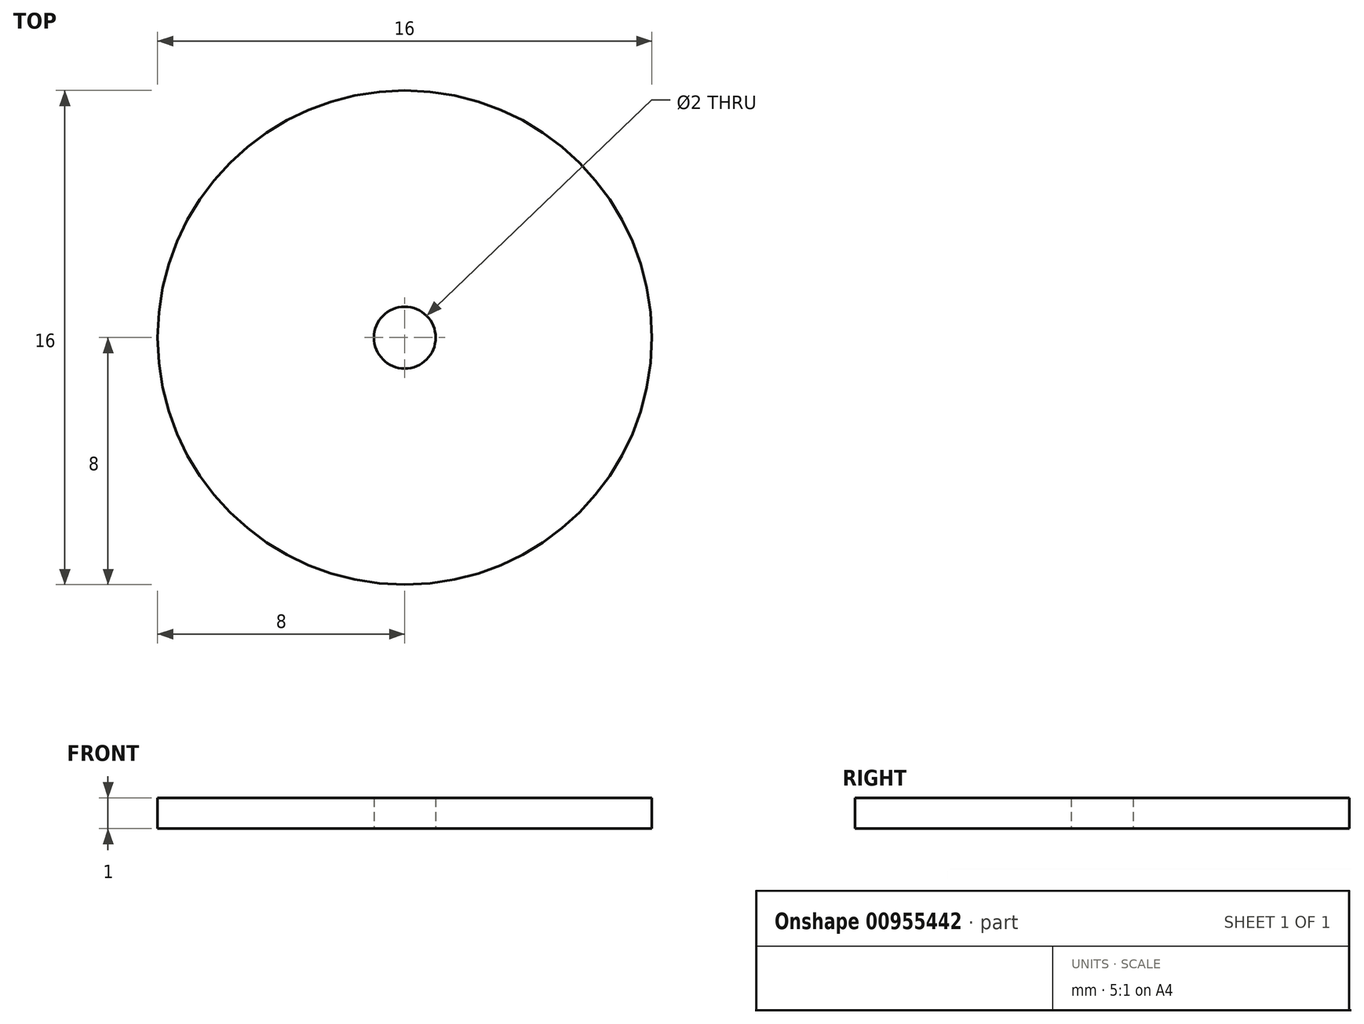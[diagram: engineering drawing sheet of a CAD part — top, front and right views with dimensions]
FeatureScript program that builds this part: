
annotation { "Feature Type Name" : "Feature", "Feature Type Description" : "" }
export const myFeature = defineFeature(function(context is Context, id is Id, definition is map)
    precondition{}
    {
        {
            var Q0;
            Q0=qCreatedBy(makeId("Front.planeOp"),FACE);
            var sketch = newSketch(context, id + "F0", { "sketchPlane" : qUnion([Q0])});
            skLineSegment(sketch, "E0", {"start": v(-1, 0) * mm, "end": v(-1, 5) * mm});
            skLineSegment(sketch, "E1", {"start": v(-1, 5) * mm, "end": v(-10, 5) * mm});
            skLineSegment(sketch, "E2", {"start": v(-10, 5) * mm, "end": v(-10, 0) * mm});
            skLineSegment(sketch, "E3", {"start": v(-10, 0) * mm, "end": v(-1, 0) * mm});
            skLineSegment(sketch, "E4", {"start": v(0, -1.6) * mm, "end": v(0, 6.24) * mm, "construction": true});
            skLineSegment(sketch, "E5.bottom", {"start": v(-1, 0) * mm, "end": v(-8, 0) * mm});
            skLineSegment(sketch, "E5.top", {"start": v(-1, 1) * mm, "end": v(-8, 1) * mm});
            skLineSegment(sketch, "E5.left", {"start": v(-1, 0) * mm, "end": v(-1, 1) * mm});
            skLineSegment(sketch, "E5.right", {"start": v(-8, 0) * mm, "end": v(-8, 1) * mm});
            skSolve(sketch);
        }
        {
            var Q0;
            Q0=makeQuery(id+"F0.imprint","IMPRINT",FACE,{"disambiguationData":[TD([[makeQuery(id+"F0.imprint","IMPRINT",EDGE,{"derivedFrom":sQuery(id+"F0.wireOp",EDGE,"E0")}),1.0]])]});
            var Q1;
            Q1=sQuery(id+"F0.wireOp",EDGE,"E4");
            revolve(context, id + "F1", {"surfaceOperationType" : NewSurfaceOperationType.NEW, "entities" : qUnion([Q0]), "axis" : qUnion([Q1]), "revolveType" : RevolveType.FULL});
        }
    });
